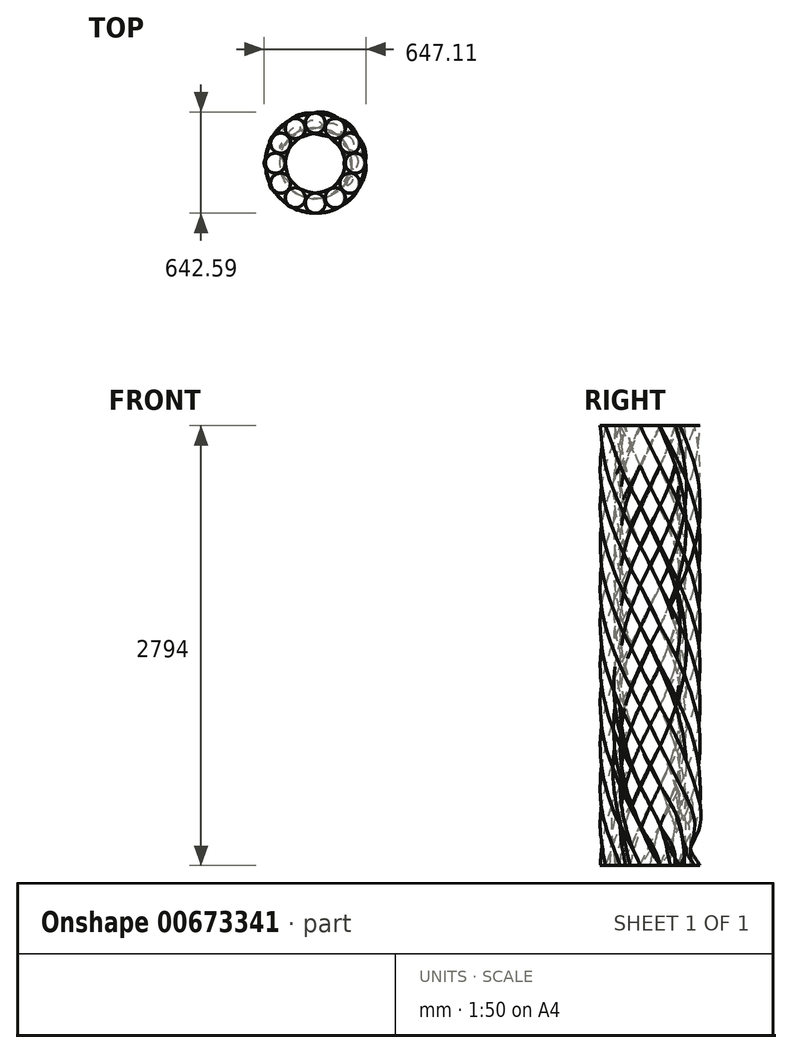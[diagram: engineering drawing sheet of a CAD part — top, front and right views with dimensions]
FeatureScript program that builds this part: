
annotation { "Feature Type Name" : "Feature", "Feature Type Description" : "" }
export const myFeature = defineFeature(function(context is Context, id is Id, definition is map)
    precondition{}
    {
        {
            var Q0;
            Q0=qCreatedBy(makeId("Top.planeOp"),FACE);
            cPlane(context, id + "F0", {"entities" : qUnion([Q0]), "cplaneType" : CPlaneType.OFFSET, "offset" : 254 * mm, "width" : 152.4 * mm, "height" : 152.4 * mm});
        }
        {
            var Q0;
            Q0=qCreatedBy(id+"F0.planeOp",FACE);
            cPlane(context, id + "F1", {"entities" : qUnion([Q0]), "cplaneType" : CPlaneType.OFFSET, "offset" : 254 * mm, "width" : 152.4 * mm, "height" : 152.4 * mm});
        }
        {
            var Q0;
            Q0=qCreatedBy(id+"F1.planeOp",FACE);
            cPlane(context, id + "F2", {"entities" : qUnion([Q0]), "cplaneType" : CPlaneType.OFFSET, "offset" : 254 * mm, "width" : 152.4 * mm, "height" : 152.4 * mm});
        }
        {
            var Q0;
            Q0=qCreatedBy(id+"F2.planeOp",FACE);
            cPlane(context, id + "F3", {"entities" : qUnion([Q0]), "cplaneType" : CPlaneType.OFFSET, "offset" : 254 * mm, "width" : 152.4 * mm, "height" : 152.4 * mm});
        }
        {
            var Q0;
            Q0=qCreatedBy(id+"F3.planeOp",FACE);
            cPlane(context, id + "F4", {"entities" : qUnion([Q0]), "cplaneType" : CPlaneType.OFFSET, "offset" : 254 * mm, "width" : 152.4 * mm, "height" : 152.4 * mm});
        }
        {
            var Q0;
            Q0=qCreatedBy(id+"F4.planeOp",FACE);
            cPlane(context, id + "F5", {"entities" : qUnion([Q0]), "cplaneType" : CPlaneType.OFFSET, "offset" : 254 * mm, "width" : 152.4 * mm, "height" : 152.4 * mm});
        }
        {
            var Q0;
            Q0=qCreatedBy(id+"F5.planeOp",FACE);
            cPlane(context, id + "F6", {"entities" : qUnion([Q0]), "cplaneType" : CPlaneType.OFFSET, "offset" : 254 * mm, "width" : 152.4 * mm, "height" : 152.4 * mm});
        }
        {
            var Q0;
            Q0=qCreatedBy(id+"F6.planeOp",FACE);
            cPlane(context, id + "F7", {"entities" : qUnion([Q0]), "cplaneType" : CPlaneType.OFFSET, "offset" : 254 * mm, "width" : 152.4 * mm, "height" : 152.4 * mm});
        }
        {
            var Q0;
            Q0=qCreatedBy(id+"F7.planeOp",FACE);
            cPlane(context, id + "F8", {"entities" : qUnion([Q0]), "cplaneType" : CPlaneType.OFFSET, "offset" : 254 * mm, "width" : 152.4 * mm, "height" : 152.4 * mm});
        }
        {
            var Q0;
            Q0=qCreatedBy(id+"F8.planeOp",FACE);
            cPlane(context, id + "F9", {"entities" : qUnion([Q0]), "cplaneType" : CPlaneType.OFFSET, "offset" : 254 * mm, "width" : 152.4 * mm, "height" : 152.4 * mm});
        }
        {
            var Q0;
            Q0=qCreatedBy(id+"F9.planeOp",FACE);
            cPlane(context, id + "F10", {"entities" : qUnion([Q0]), "cplaneType" : CPlaneType.OFFSET, "offset" : 254 * mm, "width" : 152.4 * mm, "height" : 152.4 * mm});
        }
        {
            var Q0;
            Q0=qCreatedBy(makeId("Top.planeOp"),FACE);
            var sketch = newSketch(context, id + "F11", { "sketchPlane" : qUnion([Q0])});
            skCircle(sketch, "E0", {"center": v(0, 0) * mm, "radius": 254 * mm, "construction": true});
            skLineSegment(sketch, "E1", {"start": v(13.76, 0) * mm, "end": v(-254, 0) * mm, "construction": true});
            skCircle(sketch, "E2", {"center": v(-254, 0) * mm, "radius": 63.5 * mm});
            skCircle(sketch, "E3.1.0", {"center": v(-219.97, -127) * mm, "radius": 63.5 * mm});
            skCircle(sketch, "E3.2.0", {"center": v(-127, -219.97) * mm, "radius": 63.5 * mm});
            skCircle(sketch, "E4.1.3.0", {"center": v(0, -254) * mm, "radius": 63.5 * mm});
            skCircle(sketch, "E4.1.4.0", {"center": v(127, -219.97) * mm, "radius": 63.5 * mm});
            skCircle(sketch, "E4.1.5.0", {"center": v(219.97, -127) * mm, "radius": 63.5 * mm});
            skCircle(sketch, "E4.1.6.0", {"center": v(254, 0) * mm, "radius": 63.5 * mm});
            skCircle(sketch, "E4.1.7.0", {"center": v(219.97, 127) * mm, "radius": 63.5 * mm});
            skCircle(sketch, "E4.1.8.0", {"center": v(127, 219.97) * mm, "radius": 63.5 * mm});
            skCircle(sketch, "E4.1.9.0", {"center": v(0, 254) * mm, "radius": 63.5 * mm});
            skCircle(sketch, "E4.1.10.0", {"center": v(-127, 219.97) * mm, "radius": 63.5 * mm});
            skCircle(sketch, "E4.1.11.0", {"center": v(-219.97, 127) * mm, "radius": 63.5 * mm});
            skSolve(sketch);
        }
        {
            var Q0;
            Q0=qCreatedBy(id+"F0.planeOp",FACE);
            var sketch = newSketch(context, id + "F12", { "sketchPlane" : qUnion([Q0])});
            skCircle(sketch, "E5", {"center": v(8, 0) * mm, "radius": 254 * mm, "construction": true});
            skLineSegment(sketch, "E6", {"start": v(21.76, 0) * mm, "end": v(-246, 0) * mm, "construction": true});
            skCircle(sketch, "E7", {"center": v(-246, 0) * mm, "radius": 63.5 * mm});
            skCircle(sketch, "E8.1.0", {"center": v(-211.96, -127) * mm, "radius": 63.5 * mm});
            skCircle(sketch, "E8.2.0", {"center": v(-119, -219.97) * mm, "radius": 63.5 * mm});
            skCircle(sketch, "E9.1.3.0", {"center": v(8, -254) * mm, "radius": 63.5 * mm});
            skCircle(sketch, "E9.1.4.0", {"center": v(135, -219.97) * mm, "radius": 63.5 * mm});
            skCircle(sketch, "E9.1.5.0", {"center": v(227.98, -127) * mm, "radius": 63.5 * mm});
            skCircle(sketch, "E9.1.6.0", {"center": v(262, 0) * mm, "radius": 63.5 * mm});
            skCircle(sketch, "E9.1.7.0", {"center": v(227.98, 127) * mm, "radius": 63.5 * mm});
            skCircle(sketch, "E9.1.8.0", {"center": v(135, 219.97) * mm, "radius": 63.5 * mm});
            skCircle(sketch, "E9.1.9.0", {"center": v(8, 254) * mm, "radius": 63.5 * mm});
            skCircle(sketch, "E9.1.10.0", {"center": v(-119, 219.97) * mm, "radius": 63.5 * mm});
            skCircle(sketch, "E9.1.11.0", {"center": v(-211.96, 127) * mm, "radius": 63.5 * mm});
            skSolve(sketch);
        }
        {
            var Q0;
            Q0=qCreatedBy(id+"F1.planeOp",FACE);
            var sketch = newSketch(context, id + "F13", { "sketchPlane" : qUnion([Q0])});
            skCircle(sketch, "E10", {"center": v(8, 0) * mm, "radius": 254 * mm, "construction": true});
            skLineSegment(sketch, "E11", {"start": v(21.76, 0) * mm, "end": v(-246, 0) * mm, "construction": true});
            skCircle(sketch, "E12", {"center": v(-246, 0) * mm, "radius": 63.5 * mm});
            skCircle(sketch, "E13.1.0", {"center": v(-211.96, -127) * mm, "radius": 63.5 * mm});
            skCircle(sketch, "E13.2.0", {"center": v(-119, -219.97) * mm, "radius": 63.5 * mm});
            skCircle(sketch, "E14.1.3.0", {"center": v(8, -254) * mm, "radius": 63.5 * mm});
            skCircle(sketch, "E14.1.4.0", {"center": v(135, -219.97) * mm, "radius": 63.5 * mm});
            skCircle(sketch, "E14.1.5.0", {"center": v(227.98, -127) * mm, "radius": 63.5 * mm});
            skCircle(sketch, "E14.1.6.0", {"center": v(262, 0) * mm, "radius": 63.5 * mm});
            skCircle(sketch, "E14.1.7.0", {"center": v(227.98, 127) * mm, "radius": 63.5 * mm});
            skCircle(sketch, "E14.1.8.0", {"center": v(135, 219.97) * mm, "radius": 63.5 * mm});
            skCircle(sketch, "E14.1.9.0", {"center": v(8, 254) * mm, "radius": 63.5 * mm});
            skCircle(sketch, "E14.1.10.0", {"center": v(-119, 219.97) * mm, "radius": 63.5 * mm});
            skCircle(sketch, "E14.1.11.0", {"center": v(-211.96, 127) * mm, "radius": 63.5 * mm});
            skSolve(sketch);
        }
        {
            var Q0;
            Q0=qCreatedBy(id+"F2.planeOp",FACE);
            var sketch = newSketch(context, id + "F14", { "sketchPlane" : qUnion([Q0])});
            skCircle(sketch, "E15", {"center": v(8, 0) * mm, "radius": 254 * mm, "construction": true});
            skLineSegment(sketch, "E16", {"start": v(21.76, 0) * mm, "end": v(-246, 0) * mm, "construction": true});
            skCircle(sketch, "E17", {"center": v(-246, 0) * mm, "radius": 63.5 * mm});
            skCircle(sketch, "E18.1.0", {"center": v(-211.96, -127) * mm, "radius": 63.5 * mm});
            skCircle(sketch, "E18.2.0", {"center": v(-119, -219.97) * mm, "radius": 63.5 * mm});
            skCircle(sketch, "E19.1.3.0", {"center": v(8, -254) * mm, "radius": 63.5 * mm});
            skCircle(sketch, "E19.1.4.0", {"center": v(135, -219.97) * mm, "radius": 63.5 * mm});
            skCircle(sketch, "E19.1.5.0", {"center": v(227.98, -127) * mm, "radius": 63.5 * mm});
            skCircle(sketch, "E19.1.6.0", {"center": v(262, 0) * mm, "radius": 63.5 * mm});
            skCircle(sketch, "E19.1.7.0", {"center": v(227.98, 127) * mm, "radius": 63.5 * mm});
            skCircle(sketch, "E19.1.8.0", {"center": v(135, 219.97) * mm, "radius": 63.5 * mm});
            skCircle(sketch, "E19.1.9.0", {"center": v(8, 254) * mm, "radius": 63.5 * mm});
            skCircle(sketch, "E19.1.10.0", {"center": v(-119, 219.97) * mm, "radius": 63.5 * mm});
            skCircle(sketch, "E19.1.11.0", {"center": v(-211.96, 127) * mm, "radius": 63.5 * mm});
            skSolve(sketch);
        }
        {
            var Q0;
            Q0=qCreatedBy(id+"F3.planeOp",FACE);
            var sketch = newSketch(context, id + "F15", { "sketchPlane" : qUnion([Q0])});
            skCircle(sketch, "E20", {"center": v(8, 0) * mm, "radius": 254 * mm, "construction": true});
            skLineSegment(sketch, "E21", {"start": v(21.76, 0) * mm, "end": v(-246, 0) * mm, "construction": true});
            skCircle(sketch, "E22", {"center": v(-246, 0) * mm, "radius": 63.5 * mm});
            skCircle(sketch, "E23.1.0", {"center": v(-211.96, -127) * mm, "radius": 63.5 * mm});
            skCircle(sketch, "E23.2.0", {"center": v(-119, -219.97) * mm, "radius": 63.5 * mm});
            skCircle(sketch, "E24.1.3.0", {"center": v(8, -254) * mm, "radius": 63.5 * mm});
            skCircle(sketch, "E24.1.4.0", {"center": v(135, -219.97) * mm, "radius": 63.5 * mm});
            skCircle(sketch, "E24.1.5.0", {"center": v(227.98, -127) * mm, "radius": 63.5 * mm});
            skCircle(sketch, "E24.1.6.0", {"center": v(262, 0) * mm, "radius": 63.5 * mm});
            skCircle(sketch, "E24.1.7.0", {"center": v(227.98, 127) * mm, "radius": 63.5 * mm});
            skCircle(sketch, "E24.1.8.0", {"center": v(135, 219.97) * mm, "radius": 63.5 * mm});
            skCircle(sketch, "E24.1.9.0", {"center": v(8, 254) * mm, "radius": 63.5 * mm});
            skCircle(sketch, "E24.1.10.0", {"center": v(-119, 219.97) * mm, "radius": 63.5 * mm});
            skCircle(sketch, "E24.1.11.0", {"center": v(-211.96, 127) * mm, "radius": 63.5 * mm});
            skSolve(sketch);
        }
        {
            var Q0;
            Q0=qCreatedBy(id+"F4.planeOp",FACE);
            var sketch = newSketch(context, id + "F16", { "sketchPlane" : qUnion([Q0])});
            skCircle(sketch, "E25", {"center": v(8, 0) * mm, "radius": 254 * mm, "construction": true});
            skLineSegment(sketch, "E26", {"start": v(21.76, 0) * mm, "end": v(-246, 0) * mm, "construction": true});
            skCircle(sketch, "E27", {"center": v(-246, 0) * mm, "radius": 63.5 * mm});
            skCircle(sketch, "E28.1.0", {"center": v(-211.96, -127) * mm, "radius": 63.5 * mm});
            skCircle(sketch, "E28.2.0", {"center": v(-119, -219.97) * mm, "radius": 63.5 * mm});
            skCircle(sketch, "E29.1.3.0", {"center": v(8, -254) * mm, "radius": 63.5 * mm});
            skCircle(sketch, "E29.1.4.0", {"center": v(135, -219.97) * mm, "radius": 63.5 * mm});
            skCircle(sketch, "E29.1.5.0", {"center": v(227.98, -127) * mm, "radius": 63.5 * mm});
            skCircle(sketch, "E29.1.6.0", {"center": v(262, 0) * mm, "radius": 63.5 * mm});
            skCircle(sketch, "E29.1.7.0", {"center": v(227.98, 127) * mm, "radius": 63.5 * mm});
            skCircle(sketch, "E29.1.8.0", {"center": v(135, 219.97) * mm, "radius": 63.5 * mm});
            skCircle(sketch, "E29.1.9.0", {"center": v(8, 254) * mm, "radius": 63.5 * mm});
            skCircle(sketch, "E29.1.10.0", {"center": v(-119, 219.97) * mm, "radius": 63.5 * mm});
            skCircle(sketch, "E29.1.11.0", {"center": v(-211.96, 127) * mm, "radius": 63.5 * mm});
            skSolve(sketch);
        }
        {
            var Q0;
            Q0=qCreatedBy(id+"F5.planeOp",FACE);
            var sketch = newSketch(context, id + "F17", { "sketchPlane" : qUnion([Q0])});
            skCircle(sketch, "E30", {"center": v(8, 0) * mm, "radius": 254 * mm, "construction": true});
            skLineSegment(sketch, "E31", {"start": v(21.76, 0) * mm, "end": v(-246, 0) * mm, "construction": true});
            skCircle(sketch, "E32", {"center": v(-246, 0) * mm, "radius": 63.5 * mm});
            skCircle(sketch, "E33.1.0", {"center": v(-211.96, -127) * mm, "radius": 63.5 * mm});
            skCircle(sketch, "E33.2.0", {"center": v(-119, -219.97) * mm, "radius": 63.5 * mm});
            skCircle(sketch, "E34.1.3.0", {"center": v(8, -254) * mm, "radius": 63.5 * mm});
            skCircle(sketch, "E34.1.4.0", {"center": v(135, -219.97) * mm, "radius": 63.5 * mm});
            skCircle(sketch, "E34.1.5.0", {"center": v(227.98, -127) * mm, "radius": 63.5 * mm});
            skCircle(sketch, "E34.1.6.0", {"center": v(262, 0) * mm, "radius": 63.5 * mm});
            skCircle(sketch, "E34.1.7.0", {"center": v(227.98, 127) * mm, "radius": 63.5 * mm});
            skCircle(sketch, "E34.1.8.0", {"center": v(135, 219.97) * mm, "radius": 63.5 * mm});
            skCircle(sketch, "E34.1.9.0", {"center": v(8, 254) * mm, "radius": 63.5 * mm});
            skCircle(sketch, "E34.1.10.0", {"center": v(-119, 219.97) * mm, "radius": 63.5 * mm});
            skCircle(sketch, "E34.1.11.0", {"center": v(-211.96, 127) * mm, "radius": 63.5 * mm});
            skSolve(sketch);
        }
        {
            var Q0;
            Q0=qCreatedBy(id+"F6.planeOp",FACE);
            var sketch = newSketch(context, id + "F18", { "sketchPlane" : qUnion([Q0])});
            skCircle(sketch, "E35", {"center": v(8, 0) * mm, "radius": 254 * mm, "construction": true});
            skLineSegment(sketch, "E36", {"start": v(21.76, 0) * mm, "end": v(-246, 0) * mm, "construction": true});
            skCircle(sketch, "E37", {"center": v(-246, 0) * mm, "radius": 63.5 * mm});
            skCircle(sketch, "E38.1.0", {"center": v(-211.96, -127) * mm, "radius": 63.5 * mm});
            skCircle(sketch, "E38.2.0", {"center": v(-119, -219.97) * mm, "radius": 63.5 * mm});
            skCircle(sketch, "E39.1.3.0", {"center": v(8, -254) * mm, "radius": 63.5 * mm});
            skCircle(sketch, "E39.1.4.0", {"center": v(135, -219.97) * mm, "radius": 63.5 * mm});
            skCircle(sketch, "E39.1.5.0", {"center": v(227.98, -127) * mm, "radius": 63.5 * mm});
            skCircle(sketch, "E39.1.6.0", {"center": v(262, 0) * mm, "radius": 63.5 * mm});
            skCircle(sketch, "E39.1.7.0", {"center": v(227.98, 127) * mm, "radius": 63.5 * mm});
            skCircle(sketch, "E39.1.8.0", {"center": v(135, 219.97) * mm, "radius": 63.5 * mm});
            skCircle(sketch, "E39.1.9.0", {"center": v(8, 254) * mm, "radius": 63.5 * mm});
            skCircle(sketch, "E39.1.10.0", {"center": v(-119, 219.97) * mm, "radius": 63.5 * mm});
            skCircle(sketch, "E39.1.11.0", {"center": v(-211.96, 127) * mm, "radius": 63.5 * mm});
            skSolve(sketch);
        }
        {
            var Q0;
            Q0=qCreatedBy(id+"F7.planeOp",FACE);
            var sketch = newSketch(context, id + "F19", { "sketchPlane" : qUnion([Q0])});
            skCircle(sketch, "E40", {"center": v(8, 0) * mm, "radius": 254 * mm, "construction": true});
            skLineSegment(sketch, "E41", {"start": v(21.76, 0) * mm, "end": v(-246, 0) * mm, "construction": true});
            skCircle(sketch, "E42", {"center": v(-246, 0) * mm, "radius": 63.5 * mm});
            skCircle(sketch, "E43.1.0", {"center": v(-211.96, -127) * mm, "radius": 63.5 * mm});
            skCircle(sketch, "E43.2.0", {"center": v(-119, -219.97) * mm, "radius": 63.5 * mm});
            skCircle(sketch, "E44.1.3.0", {"center": v(8, -254) * mm, "radius": 63.5 * mm});
            skCircle(sketch, "E44.1.4.0", {"center": v(135, -219.97) * mm, "radius": 63.5 * mm});
            skCircle(sketch, "E44.1.5.0", {"center": v(227.98, -127) * mm, "radius": 63.5 * mm});
            skCircle(sketch, "E44.1.6.0", {"center": v(262, 0) * mm, "radius": 63.5 * mm});
            skCircle(sketch, "E44.1.7.0", {"center": v(227.98, 127) * mm, "radius": 63.5 * mm});
            skCircle(sketch, "E44.1.8.0", {"center": v(135, 219.97) * mm, "radius": 63.5 * mm});
            skCircle(sketch, "E44.1.9.0", {"center": v(8, 254) * mm, "radius": 63.5 * mm});
            skCircle(sketch, "E44.1.10.0", {"center": v(-119, 219.97) * mm, "radius": 63.5 * mm});
            skCircle(sketch, "E44.1.11.0", {"center": v(-211.96, 127) * mm, "radius": 63.5 * mm});
            skSolve(sketch);
        }
        {
            var Q0;
            Q0=qCreatedBy(id+"F8.planeOp",FACE);
            var sketch = newSketch(context, id + "F20", { "sketchPlane" : qUnion([Q0])});
            skCircle(sketch, "E45", {"center": v(8, 0) * mm, "radius": 254 * mm, "construction": true});
            skLineSegment(sketch, "E46", {"start": v(21.76, 0) * mm, "end": v(-246, 0) * mm, "construction": true});
            skCircle(sketch, "E47", {"center": v(-246, 0) * mm, "radius": 63.5 * mm});
            skCircle(sketch, "E48.1.0", {"center": v(-211.96, -127) * mm, "radius": 63.5 * mm});
            skCircle(sketch, "E48.2.0", {"center": v(-119, -219.97) * mm, "radius": 63.5 * mm});
            skCircle(sketch, "E49.1.3.0", {"center": v(8, -254) * mm, "radius": 63.5 * mm});
            skCircle(sketch, "E49.1.4.0", {"center": v(135, -219.97) * mm, "radius": 63.5 * mm});
            skCircle(sketch, "E49.1.5.0", {"center": v(227.98, -127) * mm, "radius": 63.5 * mm});
            skCircle(sketch, "E49.1.6.0", {"center": v(262, 0) * mm, "radius": 63.5 * mm});
            skCircle(sketch, "E49.1.7.0", {"center": v(227.98, 127) * mm, "radius": 63.5 * mm});
            skCircle(sketch, "E49.1.8.0", {"center": v(135, 219.97) * mm, "radius": 63.5 * mm});
            skCircle(sketch, "E49.1.9.0", {"center": v(8, 254) * mm, "radius": 63.5 * mm});
            skCircle(sketch, "E49.1.10.0", {"center": v(-119, 219.97) * mm, "radius": 63.5 * mm});
            skCircle(sketch, "E49.1.11.0", {"center": v(-211.96, 127) * mm, "radius": 63.5 * mm});
            skSolve(sketch);
        }
        {
            var Q0;
            Q0=qCreatedBy(id+"F9.planeOp",FACE);
            var sketch = newSketch(context, id + "F21", { "sketchPlane" : qUnion([Q0])});
            skCircle(sketch, "E50", {"center": v(8, 0) * mm, "radius": 254 * mm, "construction": true});
            skLineSegment(sketch, "E51", {"start": v(21.76, 0) * mm, "end": v(-246, 0) * mm, "construction": true});
            skCircle(sketch, "E52", {"center": v(-246, 0) * mm, "radius": 63.5 * mm});
            skCircle(sketch, "E53.1.0", {"center": v(-211.96, -127) * mm, "radius": 63.5 * mm});
            skCircle(sketch, "E53.2.0", {"center": v(-119, -219.97) * mm, "radius": 63.5 * mm});
            skCircle(sketch, "E54.1.3.0", {"center": v(8, -254) * mm, "radius": 63.5 * mm});
            skCircle(sketch, "E54.1.4.0", {"center": v(135, -219.97) * mm, "radius": 63.5 * mm});
            skCircle(sketch, "E54.1.5.0", {"center": v(227.98, -127) * mm, "radius": 63.5 * mm});
            skCircle(sketch, "E54.1.6.0", {"center": v(262, 0) * mm, "radius": 63.5 * mm});
            skCircle(sketch, "E54.1.7.0", {"center": v(227.98, 127) * mm, "radius": 63.5 * mm});
            skCircle(sketch, "E54.1.8.0", {"center": v(135, 219.97) * mm, "radius": 63.5 * mm});
            skCircle(sketch, "E54.1.9.0", {"center": v(8, 254) * mm, "radius": 63.5 * mm});
            skCircle(sketch, "E54.1.10.0", {"center": v(-119, 219.97) * mm, "radius": 63.5 * mm});
            skCircle(sketch, "E54.1.11.0", {"center": v(-211.96, 127) * mm, "radius": 63.5 * mm});
            skSolve(sketch);
        }
        {
            var Q0;
            Q0=qCreatedBy(id+"F10.planeOp",FACE);
            var sketch = newSketch(context, id + "F22", { "sketchPlane" : qUnion([Q0])});
            skCircle(sketch, "E55", {"center": v(8, 0) * mm, "radius": 254 * mm, "construction": true});
            skLineSegment(sketch, "E56", {"start": v(21.76, 0) * mm, "end": v(-246, 0) * mm, "construction": true});
            skCircle(sketch, "E57", {"center": v(-246, 0) * mm, "radius": 63.5 * mm});
            skCircle(sketch, "E58.1.0", {"center": v(-211.96, -127) * mm, "radius": 63.5 * mm});
            skCircle(sketch, "E58.2.0", {"center": v(-119, -219.97) * mm, "radius": 63.5 * mm});
            skCircle(sketch, "E59.1.3.0", {"center": v(8, -254) * mm, "radius": 63.5 * mm});
            skCircle(sketch, "E59.1.4.0", {"center": v(135, -219.97) * mm, "radius": 63.5 * mm});
            skCircle(sketch, "E59.1.5.0", {"center": v(227.98, -127) * mm, "radius": 63.5 * mm});
            skCircle(sketch, "E59.1.6.0", {"center": v(262, 0) * mm, "radius": 63.5 * mm});
            skCircle(sketch, "E59.1.7.0", {"center": v(227.98, 127) * mm, "radius": 63.5 * mm});
            skCircle(sketch, "E59.1.8.0", {"center": v(135, 219.97) * mm, "radius": 63.5 * mm});
            skCircle(sketch, "E59.1.9.0", {"center": v(8, 254) * mm, "radius": 63.5 * mm});
            skCircle(sketch, "E59.1.10.0", {"center": v(-119, 219.97) * mm, "radius": 63.5 * mm});
            skCircle(sketch, "E59.1.11.0", {"center": v(-211.96, 127) * mm, "radius": 63.5 * mm});
            skSolve(sketch);
        }
        {
            var Q0;
            Q0=makeQuery(id+"F11.imprint","IMPRINT",FACE,{"disambiguationData":[TD([[makeQuery(id+"F11.imprint","IMPRINT",EDGE,{"derivedFrom":sQuery(id+"F11.wireOp",EDGE,"E2")}),1.0]])]});
            var Q1;
            Q1=makeQuery(id+"F12.imprint","IMPRINT",FACE,{"disambiguationData":[TD([[makeQuery(id+"F12.imprint","IMPRINT",EDGE,{"derivedFrom":sQuery(id+"F12.wireOp",EDGE,"E9.1.11.0")}),1.0]])]});
            var Q2;
            Q2=makeQuery(id+"F13.imprint","IMPRINT",FACE,{"disambiguationData":[TD([[makeQuery(id+"F13.imprint","IMPRINT",EDGE,{"derivedFrom":sQuery(id+"F13.wireOp",EDGE,"E14.1.10.0")}),1.0]])]});
            var Q3;
            Q3=makeQuery(id+"F14.imprint","IMPRINT",FACE,{"disambiguationData":[TD([[makeQuery(id+"F14.imprint","IMPRINT",EDGE,{"derivedFrom":sQuery(id+"F14.wireOp",EDGE,"E19.1.9.0")}),1.0]])]});
            var Q4;
            Q4=makeQuery(id+"F15.imprint","IMPRINT",FACE,{"disambiguationData":[TD([[makeQuery(id+"F15.imprint","IMPRINT",EDGE,{"derivedFrom":sQuery(id+"F15.wireOp",EDGE,"E24.1.8.0")}),1.0]])]});
            var Q5;
            Q5=makeQuery(id+"F16.imprint","IMPRINT",FACE,{"disambiguationData":[TD([[makeQuery(id+"F16.imprint","IMPRINT",EDGE,{"derivedFrom":sQuery(id+"F16.wireOp",EDGE,"E29.1.7.0")}),1.0]])]});
            var Q6;
            Q6=makeQuery(id+"F17.imprint","IMPRINT",FACE,{"disambiguationData":[TD([[makeQuery(id+"F17.imprint","IMPRINT",EDGE,{"derivedFrom":sQuery(id+"F17.wireOp",EDGE,"E34.1.6.0")}),1.0]])]});
            var Q7;
            Q7=makeQuery(id+"F18.imprint","IMPRINT",FACE,{"disambiguationData":[TD([[makeQuery(id+"F18.imprint","IMPRINT",EDGE,{"derivedFrom":sQuery(id+"F18.wireOp",EDGE,"E39.1.5.0")}),1.0]])]});
            var Q8;
            Q8=makeQuery(id+"F19.imprint","IMPRINT",FACE,{"disambiguationData":[TD([[makeQuery(id+"F19.imprint","IMPRINT",EDGE,{"derivedFrom":sQuery(id+"F19.wireOp",EDGE,"E44.1.4.0")}),1.0]])]});
            var Q9;
            Q9=makeQuery(id+"F20.imprint","IMPRINT",FACE,{"disambiguationData":[TD([[makeQuery(id+"F20.imprint","IMPRINT",EDGE,{"derivedFrom":sQuery(id+"F20.wireOp",EDGE,"E49.1.3.0")}),1.0]])]});
            var Q10;
            Q10=makeQuery(id+"F21.imprint","IMPRINT",FACE,{"disambiguationData":[TD([[makeQuery(id+"F21.imprint","IMPRINT",EDGE,{"derivedFrom":sQuery(id+"F21.wireOp",EDGE,"E53.2.0")}),1.0]])]});
            var Q11;
            Q11=makeQuery(id+"F22.imprint","IMPRINT",FACE,{"disambiguationData":[TD([[makeQuery(id+"F22.imprint","IMPRINT",EDGE,{"derivedFrom":sQuery(id+"F22.wireOp",EDGE,"E58.1.0")}),1.0]])]});
            loft(context, id + "F23", {"sheetProfilesArray" : [{ "sheetProfileEntities" : qUnion([Q0]) }, { "sheetProfileEntities" : qUnion([Q1]) }, { "sheetProfileEntities" : qUnion([Q2]) }, { "sheetProfileEntities" : qUnion([Q3]) }, { "sheetProfileEntities" : qUnion([Q4]) }, { "sheetProfileEntities" : qUnion([Q5]) }, { "sheetProfileEntities" : qUnion([Q6]) }, { "sheetProfileEntities" : qUnion([Q7]) }, { "sheetProfileEntities" : qUnion([Q8]) }, { "sheetProfileEntities" : qUnion([Q9]) }, { "sheetProfileEntities" : qUnion([Q10]) }, { "sheetProfileEntities" : qUnion([Q11]) }]});
        }
        {
            var Q1;
            Q1=makeQuery(id+"F11.imprint","IMPRINT",FACE,{"disambiguationData":[TD([[makeQuery(id+"F11.imprint","IMPRINT",EDGE,{"derivedFrom":sQuery(id+"F11.wireOp",EDGE,"E4.1.11.0")}),1.0]])]});
            var Q2;
            Q2=makeQuery(id+"F12.imprint","IMPRINT",FACE,{"disambiguationData":[TD([[makeQuery(id+"F12.imprint","IMPRINT",EDGE,{"derivedFrom":sQuery(id+"F12.wireOp",EDGE,"E9.1.10.0")}),1.0]])]});
            var Q3;
            Q3=makeQuery(id+"F13.imprint","IMPRINT",FACE,{"disambiguationData":[TD([[makeQuery(id+"F13.imprint","IMPRINT",EDGE,{"derivedFrom":sQuery(id+"F13.wireOp",EDGE,"E14.1.9.0")}),1.0]])]});
            var Q4;
            Q4=makeQuery(id+"F14.imprint","IMPRINT",FACE,{"disambiguationData":[TD([[makeQuery(id+"F14.imprint","IMPRINT",EDGE,{"derivedFrom":sQuery(id+"F14.wireOp",EDGE,"E19.1.8.0")}),1.0]])]});
            var Q5;
            Q5=makeQuery(id+"F15.imprint","IMPRINT",FACE,{"disambiguationData":[TD([[makeQuery(id+"F15.imprint","IMPRINT",EDGE,{"derivedFrom":sQuery(id+"F15.wireOp",EDGE,"E24.1.7.0")}),1.0]])]});
            var Q6;
            Q6=makeQuery(id+"F16.imprint","IMPRINT",FACE,{"disambiguationData":[TD([[makeQuery(id+"F16.imprint","IMPRINT",EDGE,{"derivedFrom":sQuery(id+"F16.wireOp",EDGE,"E29.1.6.0")}),1.0]])]});
            var Q7;
            Q7=makeQuery(id+"F17.imprint","IMPRINT",FACE,{"disambiguationData":[TD([[makeQuery(id+"F17.imprint","IMPRINT",EDGE,{"derivedFrom":sQuery(id+"F17.wireOp",EDGE,"E34.1.5.0")}),1.0]])]});
            var Q8;
            Q8=makeQuery(id+"F18.imprint","IMPRINT",FACE,{"disambiguationData":[TD([[makeQuery(id+"F18.imprint","IMPRINT",EDGE,{"derivedFrom":sQuery(id+"F18.wireOp",EDGE,"E39.1.4.0")}),1.0]])]});
            var Q9;
            Q9=makeQuery(id+"F19.imprint","IMPRINT",FACE,{"disambiguationData":[TD([[makeQuery(id+"F19.imprint","IMPRINT",EDGE,{"derivedFrom":sQuery(id+"F19.wireOp",EDGE,"E44.1.3.0")}),1.0]])]});
            var Q10;
            Q10=makeQuery(id+"F20.imprint","IMPRINT",FACE,{"disambiguationData":[TD([[makeQuery(id+"F20.imprint","IMPRINT",EDGE,{"derivedFrom":sQuery(id+"F20.wireOp",EDGE,"E48.2.0")}),1.0]])]});
            var Q11;
            Q11=makeQuery(id+"F21.imprint","IMPRINT",FACE,{"disambiguationData":[TD([[makeQuery(id+"F21.imprint","IMPRINT",EDGE,{"derivedFrom":sQuery(id+"F21.wireOp",EDGE,"E53.1.0")}),1.0]])]});
            var Q12;
            Q12=makeQuery(id+"F22.imprint","IMPRINT",FACE,{"disambiguationData":[TD([[makeQuery(id+"F22.imprint","IMPRINT",EDGE,{"derivedFrom":sQuery(id+"F22.wireOp",EDGE,"E57")}),1.0]])]});
            loft(context, id + "F24", {"operationType" : NewBodyOperationType.ADD, "sheetProfilesArray" : [{ "sheetProfileEntities" : qUnion([Q1]) }, { "sheetProfileEntities" : qUnion([Q2]) }, { "sheetProfileEntities" : qUnion([Q3]) }, { "sheetProfileEntities" : qUnion([Q4]) }, { "sheetProfileEntities" : qUnion([Q5]) }, { "sheetProfileEntities" : qUnion([Q6]) }, { "sheetProfileEntities" : qUnion([Q7]) }, { "sheetProfileEntities" : qUnion([Q8]) }, { "sheetProfileEntities" : qUnion([Q9]) }, { "sheetProfileEntities" : qUnion([Q10]) }, { "sheetProfileEntities" : qUnion([Q11]) }, { "sheetProfileEntities" : qUnion([Q12]) }]});
        }
        {
            var Q1;
            Q1=makeQuery(id+"F11.imprint","IMPRINT",FACE,{"disambiguationData":[TD([[makeQuery(id+"F11.imprint","IMPRINT",EDGE,{"derivedFrom":sQuery(id+"F11.wireOp",EDGE,"E4.1.10.0")}),1.0]])]});
            var Q2;
            Q2=makeQuery(id+"F12.imprint","IMPRINT",FACE,{"disambiguationData":[TD([[makeQuery(id+"F12.imprint","IMPRINT",EDGE,{"derivedFrom":sQuery(id+"F12.wireOp",EDGE,"E9.1.9.0")}),1.0]])]});
            var Q3;
            Q3=makeQuery(id+"F13.imprint","IMPRINT",FACE,{"disambiguationData":[TD([[makeQuery(id+"F13.imprint","IMPRINT",EDGE,{"derivedFrom":sQuery(id+"F13.wireOp",EDGE,"E14.1.8.0")}),1.0]])]});
            var Q4;
            Q4=makeQuery(id+"F14.imprint","IMPRINT",FACE,{"disambiguationData":[TD([[makeQuery(id+"F14.imprint","IMPRINT",EDGE,{"derivedFrom":sQuery(id+"F14.wireOp",EDGE,"E19.1.7.0")}),1.0]])]});
            var Q5;
            Q5=makeQuery(id+"F15.imprint","IMPRINT",FACE,{"disambiguationData":[TD([[makeQuery(id+"F15.imprint","IMPRINT",EDGE,{"derivedFrom":sQuery(id+"F15.wireOp",EDGE,"E24.1.6.0")}),1.0]])]});
            var Q6;
            Q6=makeQuery(id+"F16.imprint","IMPRINT",FACE,{"disambiguationData":[TD([[makeQuery(id+"F16.imprint","IMPRINT",EDGE,{"derivedFrom":sQuery(id+"F16.wireOp",EDGE,"E29.1.5.0")}),1.0]])]});
            var Q7;
            Q7=makeQuery(id+"F17.imprint","IMPRINT",FACE,{"disambiguationData":[TD([[makeQuery(id+"F17.imprint","IMPRINT",EDGE,{"derivedFrom":sQuery(id+"F17.wireOp",EDGE,"E34.1.4.0")}),1.0]])]});
            var Q8;
            Q8=makeQuery(id+"F18.imprint","IMPRINT",FACE,{"disambiguationData":[TD([[makeQuery(id+"F18.imprint","IMPRINT",EDGE,{"derivedFrom":sQuery(id+"F18.wireOp",EDGE,"E39.1.3.0")}),1.0]])]});
            var Q9;
            Q9=makeQuery(id+"F19.imprint","IMPRINT",FACE,{"disambiguationData":[TD([[makeQuery(id+"F19.imprint","IMPRINT",EDGE,{"derivedFrom":sQuery(id+"F19.wireOp",EDGE,"E43.2.0")}),1.0]])]});
            var Q10;
            Q10=makeQuery(id+"F20.imprint","IMPRINT",FACE,{"disambiguationData":[TD([[makeQuery(id+"F20.imprint","IMPRINT",EDGE,{"derivedFrom":sQuery(id+"F20.wireOp",EDGE,"E48.1.0")}),1.0]])]});
            var Q11;
            Q11=makeQuery(id+"F21.imprint","IMPRINT",FACE,{"disambiguationData":[TD([[makeQuery(id+"F21.imprint","IMPRINT",EDGE,{"derivedFrom":sQuery(id+"F21.wireOp",EDGE,"E52")}),1.0]])]});
            var Q12;
            Q12=makeQuery(id+"F22.imprint","IMPRINT",FACE,{"disambiguationData":[TD([[makeQuery(id+"F22.imprint","IMPRINT",EDGE,{"derivedFrom":sQuery(id+"F22.wireOp",EDGE,"E59.1.11.0")}),1.0]])]});
            loft(context, id + "F25", {"operationType" : NewBodyOperationType.ADD, "sheetProfilesArray" : [{ "sheetProfileEntities" : qUnion([Q1]) }, { "sheetProfileEntities" : qUnion([Q2]) }, { "sheetProfileEntities" : qUnion([Q3]) }, { "sheetProfileEntities" : qUnion([Q4]) }, { "sheetProfileEntities" : qUnion([Q5]) }, { "sheetProfileEntities" : qUnion([Q6]) }, { "sheetProfileEntities" : qUnion([Q7]) }, { "sheetProfileEntities" : qUnion([Q8]) }, { "sheetProfileEntities" : qUnion([Q9]) }, { "sheetProfileEntities" : qUnion([Q10]) }, { "sheetProfileEntities" : qUnion([Q11]) }, { "sheetProfileEntities" : qUnion([Q12]) }]});
        }
        {
            var Q1;
            Q1=makeQuery(id+"F11.imprint","IMPRINT",FACE,{"disambiguationData":[TD([[makeQuery(id+"F11.imprint","IMPRINT",EDGE,{"derivedFrom":sQuery(id+"F11.wireOp",EDGE,"E4.1.9.0")}),1.0]])]});
            var Q2;
            Q2=makeQuery(id+"F12.imprint","IMPRINT",FACE,{"disambiguationData":[TD([[makeQuery(id+"F12.imprint","IMPRINT",EDGE,{"derivedFrom":sQuery(id+"F12.wireOp",EDGE,"E9.1.8.0")}),1.0]])]});
            var Q3;
            Q3=makeQuery(id+"F13.imprint","IMPRINT",FACE,{"disambiguationData":[TD([[makeQuery(id+"F13.imprint","IMPRINT",EDGE,{"derivedFrom":sQuery(id+"F13.wireOp",EDGE,"E14.1.7.0")}),1.0]])]});
            var Q4;
            Q4=makeQuery(id+"F14.imprint","IMPRINT",FACE,{"disambiguationData":[TD([[makeQuery(id+"F14.imprint","IMPRINT",EDGE,{"derivedFrom":sQuery(id+"F14.wireOp",EDGE,"E19.1.6.0")}),1.0]])]});
            var Q5;
            Q5=makeQuery(id+"F15.imprint","IMPRINT",FACE,{"disambiguationData":[TD([[makeQuery(id+"F15.imprint","IMPRINT",EDGE,{"derivedFrom":sQuery(id+"F15.wireOp",EDGE,"E24.1.5.0")}),1.0]])]});
            var Q6;
            Q6=makeQuery(id+"F16.imprint","IMPRINT",FACE,{"disambiguationData":[TD([[makeQuery(id+"F16.imprint","IMPRINT",EDGE,{"derivedFrom":sQuery(id+"F16.wireOp",EDGE,"E29.1.4.0")}),1.0]])]});
            var Q7;
            Q7=makeQuery(id+"F17.imprint","IMPRINT",FACE,{"disambiguationData":[TD([[makeQuery(id+"F17.imprint","IMPRINT",EDGE,{"derivedFrom":sQuery(id+"F17.wireOp",EDGE,"E34.1.3.0")}),1.0]])]});
            var Q8;
            Q8=makeQuery(id+"F18.imprint","IMPRINT",FACE,{"disambiguationData":[TD([[makeQuery(id+"F18.imprint","IMPRINT",EDGE,{"derivedFrom":sQuery(id+"F18.wireOp",EDGE,"E38.2.0")}),1.0]])]});
            var Q9;
            Q9=makeQuery(id+"F19.imprint","IMPRINT",FACE,{"disambiguationData":[TD([[makeQuery(id+"F19.imprint","IMPRINT",EDGE,{"derivedFrom":sQuery(id+"F19.wireOp",EDGE,"E43.1.0")}),1.0]])]});
            var Q10;
            Q10=makeQuery(id+"F20.imprint","IMPRINT",FACE,{"disambiguationData":[TD([[makeQuery(id+"F20.imprint","IMPRINT",EDGE,{"derivedFrom":sQuery(id+"F20.wireOp",EDGE,"E47")}),1.0]])]});
            var Q11;
            Q11=makeQuery(id+"F21.imprint","IMPRINT",FACE,{"disambiguationData":[TD([[makeQuery(id+"F21.imprint","IMPRINT",EDGE,{"derivedFrom":sQuery(id+"F21.wireOp",EDGE,"E54.1.11.0")}),1.0]])]});
            var Q12;
            Q12=makeQuery(id+"F22.imprint","IMPRINT",FACE,{"disambiguationData":[TD([[makeQuery(id+"F22.imprint","IMPRINT",EDGE,{"derivedFrom":sQuery(id+"F22.wireOp",EDGE,"E59.1.10.0")}),1.0]])]});
            loft(context, id + "F26", {"operationType" : NewBodyOperationType.ADD, "sheetProfilesArray" : [{ "sheetProfileEntities" : qUnion([Q1]) }, { "sheetProfileEntities" : qUnion([Q2]) }, { "sheetProfileEntities" : qUnion([Q3]) }, { "sheetProfileEntities" : qUnion([Q4]) }, { "sheetProfileEntities" : qUnion([Q5]) }, { "sheetProfileEntities" : qUnion([Q6]) }, { "sheetProfileEntities" : qUnion([Q7]) }, { "sheetProfileEntities" : qUnion([Q8]) }, { "sheetProfileEntities" : qUnion([Q9]) }, { "sheetProfileEntities" : qUnion([Q10]) }, { "sheetProfileEntities" : qUnion([Q11]) }, { "sheetProfileEntities" : qUnion([Q12]) }]});
        }
        {
            var Q1;
            Q1=makeQuery(id+"F11.imprint","IMPRINT",FACE,{"disambiguationData":[TD([[makeQuery(id+"F11.imprint","IMPRINT",EDGE,{"derivedFrom":sQuery(id+"F11.wireOp",EDGE,"E4.1.8.0")}),1.0]])]});
            var Q2;
            Q2=makeQuery(id+"F12.imprint","IMPRINT",FACE,{"disambiguationData":[TD([[makeQuery(id+"F12.imprint","IMPRINT",EDGE,{"derivedFrom":sQuery(id+"F12.wireOp",EDGE,"E9.1.7.0")}),1.0]])]});
            var Q3;
            Q3=makeQuery(id+"F13.imprint","IMPRINT",FACE,{"disambiguationData":[TD([[makeQuery(id+"F13.imprint","IMPRINT",EDGE,{"derivedFrom":sQuery(id+"F13.wireOp",EDGE,"E14.1.6.0")}),1.0]])]});
            var Q4;
            Q4=makeQuery(id+"F14.imprint","IMPRINT",FACE,{"disambiguationData":[TD([[makeQuery(id+"F14.imprint","IMPRINT",EDGE,{"derivedFrom":sQuery(id+"F14.wireOp",EDGE,"E19.1.5.0")}),1.0]])]});
            var Q5;
            Q5=makeQuery(id+"F15.imprint","IMPRINT",FACE,{"disambiguationData":[TD([[makeQuery(id+"F15.imprint","IMPRINT",EDGE,{"derivedFrom":sQuery(id+"F15.wireOp",EDGE,"E24.1.4.0")}),1.0]])]});
            var Q6;
            Q6=makeQuery(id+"F16.imprint","IMPRINT",FACE,{"disambiguationData":[TD([[makeQuery(id+"F16.imprint","IMPRINT",EDGE,{"derivedFrom":sQuery(id+"F16.wireOp",EDGE,"E29.1.3.0")}),1.0]])]});
            var Q7;
            Q7=makeQuery(id+"F17.imprint","IMPRINT",FACE,{"disambiguationData":[TD([[makeQuery(id+"F17.imprint","IMPRINT",EDGE,{"derivedFrom":sQuery(id+"F17.wireOp",EDGE,"E33.2.0")}),1.0]])]});
            var Q8;
            Q8=makeQuery(id+"F18.imprint","IMPRINT",FACE,{"disambiguationData":[TD([[makeQuery(id+"F18.imprint","IMPRINT",EDGE,{"derivedFrom":sQuery(id+"F18.wireOp",EDGE,"E38.1.0")}),1.0]])]});
            var Q9;
            Q9=makeQuery(id+"F19.imprint","IMPRINT",FACE,{"disambiguationData":[TD([[makeQuery(id+"F19.imprint","IMPRINT",EDGE,{"derivedFrom":sQuery(id+"F19.wireOp",EDGE,"E42")}),1.0]])]});
            var Q10;
            Q10=makeQuery(id+"F20.imprint","IMPRINT",FACE,{"disambiguationData":[TD([[makeQuery(id+"F20.imprint","IMPRINT",EDGE,{"derivedFrom":sQuery(id+"F20.wireOp",EDGE,"E49.1.11.0")}),1.0]])]});
            var Q11;
            Q11=makeQuery(id+"F21.imprint","IMPRINT",FACE,{"disambiguationData":[TD([[makeQuery(id+"F21.imprint","IMPRINT",EDGE,{"derivedFrom":sQuery(id+"F21.wireOp",EDGE,"E54.1.10.0")}),1.0]])]});
            var Q12;
            Q12=makeQuery(id+"F22.imprint","IMPRINT",FACE,{"disambiguationData":[TD([[makeQuery(id+"F22.imprint","IMPRINT",EDGE,{"derivedFrom":sQuery(id+"F22.wireOp",EDGE,"E59.1.9.0")}),1.0]])]});
            loft(context, id + "F27", {"operationType" : NewBodyOperationType.ADD, "sheetProfilesArray" : [{ "sheetProfileEntities" : qUnion([Q1]) }, { "sheetProfileEntities" : qUnion([Q2]) }, { "sheetProfileEntities" : qUnion([Q3]) }, { "sheetProfileEntities" : qUnion([Q4]) }, { "sheetProfileEntities" : qUnion([Q5]) }, { "sheetProfileEntities" : qUnion([Q6]) }, { "sheetProfileEntities" : qUnion([Q7]) }, { "sheetProfileEntities" : qUnion([Q8]) }, { "sheetProfileEntities" : qUnion([Q9]) }, { "sheetProfileEntities" : qUnion([Q10]) }, { "sheetProfileEntities" : qUnion([Q11]) }, { "sheetProfileEntities" : qUnion([Q12]) }]});
        }
        {
            var Q1;
            Q1=makeQuery(id+"F11.imprint","IMPRINT",FACE,{"disambiguationData":[TD([[makeQuery(id+"F11.imprint","IMPRINT",EDGE,{"derivedFrom":sQuery(id+"F11.wireOp",EDGE,"E4.1.7.0")}),1.0]])]});
            var Q2;
            Q2=makeQuery(id+"F12.imprint","IMPRINT",FACE,{"disambiguationData":[TD([[makeQuery(id+"F12.imprint","IMPRINT",EDGE,{"derivedFrom":sQuery(id+"F12.wireOp",EDGE,"E9.1.6.0")}),1.0]])]});
            var Q3;
            Q3=makeQuery(id+"F13.imprint","IMPRINT",FACE,{"disambiguationData":[TD([[makeQuery(id+"F13.imprint","IMPRINT",EDGE,{"derivedFrom":sQuery(id+"F13.wireOp",EDGE,"E14.1.5.0")}),1.0]])]});
            var Q4;
            Q4=makeQuery(id+"F14.imprint","IMPRINT",FACE,{"disambiguationData":[TD([[makeQuery(id+"F14.imprint","IMPRINT",EDGE,{"derivedFrom":sQuery(id+"F14.wireOp",EDGE,"E19.1.4.0")}),1.0]])]});
            var Q5;
            Q5=makeQuery(id+"F15.imprint","IMPRINT",FACE,{"disambiguationData":[TD([[makeQuery(id+"F15.imprint","IMPRINT",EDGE,{"derivedFrom":sQuery(id+"F15.wireOp",EDGE,"E24.1.3.0")}),1.0]])]});
            var Q6;
            Q6=makeQuery(id+"F16.imprint","IMPRINT",FACE,{"disambiguationData":[TD([[makeQuery(id+"F16.imprint","IMPRINT",EDGE,{"derivedFrom":sQuery(id+"F16.wireOp",EDGE,"E28.2.0")}),1.0]])]});
            var Q7;
            Q7=makeQuery(id+"F17.imprint","IMPRINT",FACE,{"disambiguationData":[TD([[makeQuery(id+"F17.imprint","IMPRINT",EDGE,{"derivedFrom":sQuery(id+"F17.wireOp",EDGE,"E33.1.0")}),1.0]])]});
            var Q8;
            Q8=makeQuery(id+"F18.imprint","IMPRINT",FACE,{"disambiguationData":[TD([[makeQuery(id+"F18.imprint","IMPRINT",EDGE,{"derivedFrom":sQuery(id+"F18.wireOp",EDGE,"E37")}),1.0]])]});
            var Q9;
            Q9=makeQuery(id+"F19.imprint","IMPRINT",FACE,{"disambiguationData":[TD([[makeQuery(id+"F19.imprint","IMPRINT",EDGE,{"derivedFrom":sQuery(id+"F19.wireOp",EDGE,"E44.1.11.0")}),1.0]])]});
            var Q10;
            Q10=makeQuery(id+"F20.imprint","IMPRINT",FACE,{"disambiguationData":[TD([[makeQuery(id+"F20.imprint","IMPRINT",EDGE,{"derivedFrom":sQuery(id+"F20.wireOp",EDGE,"E49.1.10.0")}),1.0]])]});
            var Q11;
            Q11=makeQuery(id+"F21.imprint","IMPRINT",FACE,{"disambiguationData":[TD([[makeQuery(id+"F21.imprint","IMPRINT",EDGE,{"derivedFrom":sQuery(id+"F21.wireOp",EDGE,"E54.1.9.0")}),1.0]])]});
            var Q12;
            Q12=makeQuery(id+"F22.imprint","IMPRINT",FACE,{"disambiguationData":[TD([[makeQuery(id+"F22.imprint","IMPRINT",EDGE,{"derivedFrom":sQuery(id+"F22.wireOp",EDGE,"E59.1.8.0")}),1.0]])]});
            loft(context, id + "F28", {"operationType" : NewBodyOperationType.ADD, "sheetProfilesArray" : [{ "sheetProfileEntities" : qUnion([Q1]) }, { "sheetProfileEntities" : qUnion([Q2]) }, { "sheetProfileEntities" : qUnion([Q3]) }, { "sheetProfileEntities" : qUnion([Q4]) }, { "sheetProfileEntities" : qUnion([Q5]) }, { "sheetProfileEntities" : qUnion([Q6]) }, { "sheetProfileEntities" : qUnion([Q7]) }, { "sheetProfileEntities" : qUnion([Q8]) }, { "sheetProfileEntities" : qUnion([Q9]) }, { "sheetProfileEntities" : qUnion([Q10]) }, { "sheetProfileEntities" : qUnion([Q11]) }, { "sheetProfileEntities" : qUnion([Q12]) }]});
        }
        {
            var Q1;
            Q1=makeQuery(id+"F11.imprint","IMPRINT",FACE,{"disambiguationData":[TD([[makeQuery(id+"F11.imprint","IMPRINT",EDGE,{"derivedFrom":sQuery(id+"F11.wireOp",EDGE,"E4.1.6.0")}),1.0]])]});
            var Q2;
            Q2=makeQuery(id+"F12.imprint","IMPRINT",FACE,{"disambiguationData":[TD([[makeQuery(id+"F12.imprint","IMPRINT",EDGE,{"derivedFrom":sQuery(id+"F12.wireOp",EDGE,"E9.1.5.0")}),1.0]])]});
            var Q3;
            Q3=makeQuery(id+"F13.imprint","IMPRINT",FACE,{"disambiguationData":[TD([[makeQuery(id+"F13.imprint","IMPRINT",EDGE,{"derivedFrom":sQuery(id+"F13.wireOp",EDGE,"E14.1.4.0")}),1.0]])]});
            var Q4;
            Q4=makeQuery(id+"F14.imprint","IMPRINT",FACE,{"disambiguationData":[TD([[makeQuery(id+"F14.imprint","IMPRINT",EDGE,{"derivedFrom":sQuery(id+"F14.wireOp",EDGE,"E19.1.3.0")}),1.0]])]});
            var Q5;
            Q5=makeQuery(id+"F15.imprint","IMPRINT",FACE,{"disambiguationData":[TD([[makeQuery(id+"F15.imprint","IMPRINT",EDGE,{"derivedFrom":sQuery(id+"F15.wireOp",EDGE,"E23.2.0")}),1.0]])]});
            var Q6;
            Q6=makeQuery(id+"F16.imprint","IMPRINT",FACE,{"disambiguationData":[TD([[makeQuery(id+"F16.imprint","IMPRINT",EDGE,{"derivedFrom":sQuery(id+"F16.wireOp",EDGE,"E28.1.0")}),1.0]])]});
            var Q7;
            Q7=makeQuery(id+"F17.imprint","IMPRINT",FACE,{"disambiguationData":[TD([[makeQuery(id+"F17.imprint","IMPRINT",EDGE,{"derivedFrom":sQuery(id+"F17.wireOp",EDGE,"E32")}),1.0]])]});
            var Q8;
            Q8=makeQuery(id+"F18.imprint","IMPRINT",FACE,{"disambiguationData":[TD([[makeQuery(id+"F18.imprint","IMPRINT",EDGE,{"derivedFrom":sQuery(id+"F18.wireOp",EDGE,"E39.1.11.0")}),1.0]])]});
            var Q9;
            Q9=makeQuery(id+"F19.imprint","IMPRINT",FACE,{"disambiguationData":[TD([[makeQuery(id+"F19.imprint","IMPRINT",EDGE,{"derivedFrom":sQuery(id+"F19.wireOp",EDGE,"E44.1.10.0")}),1.0]])]});
            var Q10;
            Q10=makeQuery(id+"F20.imprint","IMPRINT",FACE,{"disambiguationData":[TD([[makeQuery(id+"F20.imprint","IMPRINT",EDGE,{"derivedFrom":sQuery(id+"F20.wireOp",EDGE,"E49.1.9.0")}),1.0]])]});
            var Q11;
            Q11=makeQuery(id+"F21.imprint","IMPRINT",FACE,{"disambiguationData":[TD([[makeQuery(id+"F21.imprint","IMPRINT",EDGE,{"derivedFrom":sQuery(id+"F21.wireOp",EDGE,"E54.1.8.0")}),1.0]])]});
            var Q12;
            Q12=makeQuery(id+"F22.imprint","IMPRINT",FACE,{"disambiguationData":[TD([[makeQuery(id+"F22.imprint","IMPRINT",EDGE,{"derivedFrom":sQuery(id+"F22.wireOp",EDGE,"E59.1.7.0")}),1.0]])]});
            loft(context, id + "F29", {"operationType" : NewBodyOperationType.ADD, "sheetProfilesArray" : [{ "sheetProfileEntities" : qUnion([Q1]) }, { "sheetProfileEntities" : qUnion([Q2]) }, { "sheetProfileEntities" : qUnion([Q3]) }, { "sheetProfileEntities" : qUnion([Q4]) }, { "sheetProfileEntities" : qUnion([Q5]) }, { "sheetProfileEntities" : qUnion([Q6]) }, { "sheetProfileEntities" : qUnion([Q7]) }, { "sheetProfileEntities" : qUnion([Q8]) }, { "sheetProfileEntities" : qUnion([Q9]) }, { "sheetProfileEntities" : qUnion([Q10]) }, { "sheetProfileEntities" : qUnion([Q11]) }, { "sheetProfileEntities" : qUnion([Q12]) }]});
        }
        {
            var Q1;
            Q1=makeQuery(id+"F11.imprint","IMPRINT",FACE,{"disambiguationData":[TD([[makeQuery(id+"F11.imprint","IMPRINT",EDGE,{"derivedFrom":sQuery(id+"F11.wireOp",EDGE,"E4.1.5.0")}),1.0]])]});
            var Q2;
            Q2=makeQuery(id+"F12.imprint","IMPRINT",FACE,{"disambiguationData":[TD([[makeQuery(id+"F12.imprint","IMPRINT",EDGE,{"derivedFrom":sQuery(id+"F12.wireOp",EDGE,"E9.1.4.0")}),1.0]])]});
            var Q3;
            Q3=makeQuery(id+"F13.imprint","IMPRINT",FACE,{"disambiguationData":[TD([[makeQuery(id+"F13.imprint","IMPRINT",EDGE,{"derivedFrom":sQuery(id+"F13.wireOp",EDGE,"E14.1.3.0")}),1.0]])]});
            var Q4;
            Q4=makeQuery(id+"F14.imprint","IMPRINT",FACE,{"disambiguationData":[TD([[makeQuery(id+"F14.imprint","IMPRINT",EDGE,{"derivedFrom":sQuery(id+"F14.wireOp",EDGE,"E18.2.0")}),1.0]])]});
            var Q5;
            Q5=makeQuery(id+"F15.imprint","IMPRINT",FACE,{"disambiguationData":[TD([[makeQuery(id+"F15.imprint","IMPRINT",EDGE,{"derivedFrom":sQuery(id+"F15.wireOp",EDGE,"E23.1.0")}),1.0]])]});
            var Q6;
            Q6=makeQuery(id+"F16.imprint","IMPRINT",FACE,{"disambiguationData":[TD([[makeQuery(id+"F16.imprint","IMPRINT",EDGE,{"derivedFrom":sQuery(id+"F16.wireOp",EDGE,"E27")}),1.0]])]});
            var Q7;
            Q7=makeQuery(id+"F17.imprint","IMPRINT",FACE,{"disambiguationData":[TD([[makeQuery(id+"F17.imprint","IMPRINT",EDGE,{"derivedFrom":sQuery(id+"F17.wireOp",EDGE,"E34.1.11.0")}),1.0]])]});
            var Q8;
            Q8=makeQuery(id+"F18.imprint","IMPRINT",FACE,{"disambiguationData":[TD([[makeQuery(id+"F18.imprint","IMPRINT",EDGE,{"derivedFrom":sQuery(id+"F18.wireOp",EDGE,"E39.1.10.0")}),1.0]])]});
            var Q9;
            Q9=makeQuery(id+"F19.imprint","IMPRINT",FACE,{"disambiguationData":[TD([[makeQuery(id+"F19.imprint","IMPRINT",EDGE,{"derivedFrom":sQuery(id+"F19.wireOp",EDGE,"E44.1.9.0")}),1.0]])]});
            var Q10;
            Q10=makeQuery(id+"F20.imprint","IMPRINT",FACE,{"disambiguationData":[TD([[makeQuery(id+"F20.imprint","IMPRINT",EDGE,{"derivedFrom":sQuery(id+"F20.wireOp",EDGE,"E49.1.8.0")}),1.0]])]});
            var Q11;
            Q11=makeQuery(id+"F21.imprint","IMPRINT",FACE,{"disambiguationData":[TD([[makeQuery(id+"F21.imprint","IMPRINT",EDGE,{"derivedFrom":sQuery(id+"F21.wireOp",EDGE,"E54.1.7.0")}),1.0]])]});
            var Q12;
            Q12=makeQuery(id+"F22.imprint","IMPRINT",FACE,{"disambiguationData":[TD([[makeQuery(id+"F22.imprint","IMPRINT",EDGE,{"derivedFrom":sQuery(id+"F22.wireOp",EDGE,"E59.1.6.0")}),1.0]])]});
            loft(context, id + "F30", {"operationType" : NewBodyOperationType.ADD, "sheetProfilesArray" : [{ "sheetProfileEntities" : qUnion([Q1]) }, { "sheetProfileEntities" : qUnion([Q2]) }, { "sheetProfileEntities" : qUnion([Q3]) }, { "sheetProfileEntities" : qUnion([Q4]) }, { "sheetProfileEntities" : qUnion([Q5]) }, { "sheetProfileEntities" : qUnion([Q6]) }, { "sheetProfileEntities" : qUnion([Q7]) }, { "sheetProfileEntities" : qUnion([Q8]) }, { "sheetProfileEntities" : qUnion([Q9]) }, { "sheetProfileEntities" : qUnion([Q10]) }, { "sheetProfileEntities" : qUnion([Q11]) }, { "sheetProfileEntities" : qUnion([Q12]) }]});
        }
        {
            var Q1;
            Q1=makeQuery(id+"F11.imprint","IMPRINT",FACE,{"disambiguationData":[TD([[makeQuery(id+"F11.imprint","IMPRINT",EDGE,{"derivedFrom":sQuery(id+"F11.wireOp",EDGE,"E4.1.4.0")}),1.0]])]});
            var Q2;
            Q2=makeQuery(id+"F12.imprint","IMPRINT",FACE,{"disambiguationData":[TD([[makeQuery(id+"F12.imprint","IMPRINT",EDGE,{"derivedFrom":sQuery(id+"F12.wireOp",EDGE,"E9.1.3.0")}),1.0]])]});
            var Q3;
            Q3=makeQuery(id+"F13.imprint","IMPRINT",FACE,{"disambiguationData":[TD([[makeQuery(id+"F13.imprint","IMPRINT",EDGE,{"derivedFrom":sQuery(id+"F13.wireOp",EDGE,"E13.2.0")}),1.0]])]});
            var Q4;
            Q4=makeQuery(id+"F14.imprint","IMPRINT",FACE,{"disambiguationData":[TD([[makeQuery(id+"F14.imprint","IMPRINT",EDGE,{"derivedFrom":sQuery(id+"F14.wireOp",EDGE,"E18.1.0")}),1.0]])]});
            var Q5;
            Q5=makeQuery(id+"F15.imprint","IMPRINT",FACE,{"disambiguationData":[TD([[makeQuery(id+"F15.imprint","IMPRINT",EDGE,{"derivedFrom":sQuery(id+"F15.wireOp",EDGE,"E22")}),1.0]])]});
            var Q6;
            Q6=makeQuery(id+"F16.imprint","IMPRINT",FACE,{"disambiguationData":[TD([[makeQuery(id+"F16.imprint","IMPRINT",EDGE,{"derivedFrom":sQuery(id+"F16.wireOp",EDGE,"E29.1.11.0")}),1.0]])]});
            var Q7;
            Q7=makeQuery(id+"F17.imprint","IMPRINT",FACE,{"disambiguationData":[TD([[makeQuery(id+"F17.imprint","IMPRINT",EDGE,{"derivedFrom":sQuery(id+"F17.wireOp",EDGE,"E34.1.10.0")}),1.0]])]});
            var Q8;
            Q8=makeQuery(id+"F18.imprint","IMPRINT",FACE,{"disambiguationData":[TD([[makeQuery(id+"F18.imprint","IMPRINT",EDGE,{"derivedFrom":sQuery(id+"F18.wireOp",EDGE,"E39.1.9.0")}),1.0]])]});
            var Q9;
            Q9=makeQuery(id+"F19.imprint","IMPRINT",FACE,{"disambiguationData":[TD([[makeQuery(id+"F19.imprint","IMPRINT",EDGE,{"derivedFrom":sQuery(id+"F19.wireOp",EDGE,"E44.1.8.0")}),1.0]])]});
            var Q10;
            Q10=makeQuery(id+"F20.imprint","IMPRINT",FACE,{"disambiguationData":[TD([[makeQuery(id+"F20.imprint","IMPRINT",EDGE,{"derivedFrom":sQuery(id+"F20.wireOp",EDGE,"E49.1.7.0")}),1.0]])]});
            var Q11;
            Q11=makeQuery(id+"F21.imprint","IMPRINT",FACE,{"disambiguationData":[TD([[makeQuery(id+"F21.imprint","IMPRINT",EDGE,{"derivedFrom":sQuery(id+"F21.wireOp",EDGE,"E54.1.6.0")}),1.0]])]});
            var Q12;
            Q12=makeQuery(id+"F22.imprint","IMPRINT",FACE,{"disambiguationData":[TD([[makeQuery(id+"F22.imprint","IMPRINT",EDGE,{"derivedFrom":sQuery(id+"F22.wireOp",EDGE,"E59.1.5.0")}),1.0]])]});
            loft(context, id + "F31", {"operationType" : NewBodyOperationType.ADD, "sheetProfilesArray" : [{ "sheetProfileEntities" : qUnion([Q1]) }, { "sheetProfileEntities" : qUnion([Q2]) }, { "sheetProfileEntities" : qUnion([Q3]) }, { "sheetProfileEntities" : qUnion([Q4]) }, { "sheetProfileEntities" : qUnion([Q5]) }, { "sheetProfileEntities" : qUnion([Q6]) }, { "sheetProfileEntities" : qUnion([Q7]) }, { "sheetProfileEntities" : qUnion([Q8]) }, { "sheetProfileEntities" : qUnion([Q9]) }, { "sheetProfileEntities" : qUnion([Q10]) }, { "sheetProfileEntities" : qUnion([Q11]) }, { "sheetProfileEntities" : qUnion([Q12]) }]});
        }
        {
            var Q1;
            Q1=makeQuery(id+"F11.imprint","IMPRINT",FACE,{"disambiguationData":[TD([[makeQuery(id+"F11.imprint","IMPRINT",EDGE,{"derivedFrom":sQuery(id+"F11.wireOp",EDGE,"E4.1.3.0")}),1.0]])]});
            var Q2;
            Q2=makeQuery(id+"F12.imprint","IMPRINT",FACE,{"disambiguationData":[TD([[makeQuery(id+"F12.imprint","IMPRINT",EDGE,{"derivedFrom":sQuery(id+"F12.wireOp",EDGE,"E8.2.0")}),1.0]])]});
            var Q3;
            Q3=makeQuery(id+"F13.imprint","IMPRINT",FACE,{"disambiguationData":[TD([[makeQuery(id+"F13.imprint","IMPRINT",EDGE,{"derivedFrom":sQuery(id+"F13.wireOp",EDGE,"E13.1.0")}),1.0]])]});
            var Q4;
            Q4=makeQuery(id+"F14.imprint","IMPRINT",FACE,{"disambiguationData":[TD([[makeQuery(id+"F14.imprint","IMPRINT",EDGE,{"derivedFrom":sQuery(id+"F14.wireOp",EDGE,"E17")}),1.0]])]});
            var Q5;
            Q5=makeQuery(id+"F15.imprint","IMPRINT",FACE,{"disambiguationData":[TD([[makeQuery(id+"F15.imprint","IMPRINT",EDGE,{"derivedFrom":sQuery(id+"F15.wireOp",EDGE,"E24.1.11.0")}),1.0]])]});
            var Q6;
            Q6=makeQuery(id+"F16.imprint","IMPRINT",FACE,{"disambiguationData":[TD([[makeQuery(id+"F16.imprint","IMPRINT",EDGE,{"derivedFrom":sQuery(id+"F16.wireOp",EDGE,"E29.1.10.0")}),1.0]])]});
            var Q7;
            Q7=makeQuery(id+"F17.imprint","IMPRINT",FACE,{"disambiguationData":[TD([[makeQuery(id+"F17.imprint","IMPRINT",EDGE,{"derivedFrom":sQuery(id+"F17.wireOp",EDGE,"E34.1.9.0")}),1.0]])]});
            var Q8;
            Q8=makeQuery(id+"F18.imprint","IMPRINT",FACE,{"disambiguationData":[TD([[makeQuery(id+"F18.imprint","IMPRINT",EDGE,{"derivedFrom":sQuery(id+"F18.wireOp",EDGE,"E39.1.8.0")}),1.0]])]});
            var Q9;
            Q9=makeQuery(id+"F19.imprint","IMPRINT",FACE,{"disambiguationData":[TD([[makeQuery(id+"F19.imprint","IMPRINT",EDGE,{"derivedFrom":sQuery(id+"F19.wireOp",EDGE,"E44.1.7.0")}),1.0]])]});
            var Q10;
            Q10=makeQuery(id+"F20.imprint","IMPRINT",FACE,{"disambiguationData":[TD([[makeQuery(id+"F20.imprint","IMPRINT",EDGE,{"derivedFrom":sQuery(id+"F20.wireOp",EDGE,"E49.1.6.0")}),1.0]])]});
            var Q11;
            Q11=makeQuery(id+"F21.imprint","IMPRINT",FACE,{"disambiguationData":[TD([[makeQuery(id+"F21.imprint","IMPRINT",EDGE,{"derivedFrom":sQuery(id+"F21.wireOp",EDGE,"E54.1.5.0")}),1.0]])]});
            var Q12;
            Q12=makeQuery(id+"F22.imprint","IMPRINT",FACE,{"disambiguationData":[TD([[makeQuery(id+"F22.imprint","IMPRINT",EDGE,{"derivedFrom":sQuery(id+"F22.wireOp",EDGE,"E59.1.4.0")}),1.0]])]});
            loft(context, id + "F32", {"operationType" : NewBodyOperationType.ADD, "sheetProfilesArray" : [{ "sheetProfileEntities" : qUnion([Q1]) }, { "sheetProfileEntities" : qUnion([Q2]) }, { "sheetProfileEntities" : qUnion([Q3]) }, { "sheetProfileEntities" : qUnion([Q4]) }, { "sheetProfileEntities" : qUnion([Q5]) }, { "sheetProfileEntities" : qUnion([Q6]) }, { "sheetProfileEntities" : qUnion([Q7]) }, { "sheetProfileEntities" : qUnion([Q8]) }, { "sheetProfileEntities" : qUnion([Q9]) }, { "sheetProfileEntities" : qUnion([Q10]) }, { "sheetProfileEntities" : qUnion([Q11]) }, { "sheetProfileEntities" : qUnion([Q12]) }]});
        }
        {
            var Q1;
            Q1=makeQuery(id+"F11.imprint","IMPRINT",FACE,{"disambiguationData":[TD([[makeQuery(id+"F11.imprint","IMPRINT",EDGE,{"derivedFrom":sQuery(id+"F11.wireOp",EDGE,"E3.2.0")}),1.0]])]});
            var Q2;
            Q2=makeQuery(id+"F12.imprint","IMPRINT",FACE,{"disambiguationData":[TD([[makeQuery(id+"F12.imprint","IMPRINT",EDGE,{"derivedFrom":sQuery(id+"F12.wireOp",EDGE,"E8.1.0")}),1.0]])]});
            var Q3;
            Q3=makeQuery(id+"F13.imprint","IMPRINT",FACE,{"disambiguationData":[TD([[makeQuery(id+"F13.imprint","IMPRINT",EDGE,{"derivedFrom":sQuery(id+"F13.wireOp",EDGE,"E12")}),1.0]])]});
            var Q4;
            Q4=makeQuery(id+"F14.imprint","IMPRINT",FACE,{"disambiguationData":[TD([[makeQuery(id+"F14.imprint","IMPRINT",EDGE,{"derivedFrom":sQuery(id+"F14.wireOp",EDGE,"E19.1.11.0")}),1.0]])]});
            var Q5;
            Q5=makeQuery(id+"F15.imprint","IMPRINT",FACE,{"disambiguationData":[TD([[makeQuery(id+"F15.imprint","IMPRINT",EDGE,{"derivedFrom":sQuery(id+"F15.wireOp",EDGE,"E24.1.10.0")}),1.0]])]});
            var Q6;
            Q6=makeQuery(id+"F16.imprint","IMPRINT",FACE,{"disambiguationData":[TD([[makeQuery(id+"F16.imprint","IMPRINT",EDGE,{"derivedFrom":sQuery(id+"F16.wireOp",EDGE,"E29.1.9.0")}),1.0]])]});
            var Q7;
            Q7=makeQuery(id+"F17.imprint","IMPRINT",FACE,{"disambiguationData":[TD([[makeQuery(id+"F17.imprint","IMPRINT",EDGE,{"derivedFrom":sQuery(id+"F17.wireOp",EDGE,"E34.1.8.0")}),1.0]])]});
            var Q8;
            Q8=makeQuery(id+"F18.imprint","IMPRINT",FACE,{"disambiguationData":[TD([[makeQuery(id+"F18.imprint","IMPRINT",EDGE,{"derivedFrom":sQuery(id+"F18.wireOp",EDGE,"E39.1.7.0")}),1.0]])]});
            var Q9;
            Q9=makeQuery(id+"F19.imprint","IMPRINT",FACE,{"disambiguationData":[TD([[makeQuery(id+"F19.imprint","IMPRINT",EDGE,{"derivedFrom":sQuery(id+"F19.wireOp",EDGE,"E44.1.6.0")}),1.0]])]});
            var Q10;
            Q10=makeQuery(id+"F20.imprint","IMPRINT",FACE,{"disambiguationData":[TD([[makeQuery(id+"F20.imprint","IMPRINT",EDGE,{"derivedFrom":sQuery(id+"F20.wireOp",EDGE,"E49.1.5.0")}),1.0]])]});
            var Q11;
            Q11=makeQuery(id+"F21.imprint","IMPRINT",FACE,{"disambiguationData":[TD([[makeQuery(id+"F21.imprint","IMPRINT",EDGE,{"derivedFrom":sQuery(id+"F21.wireOp",EDGE,"E54.1.4.0")}),1.0]])]});
            var Q12;
            Q12=makeQuery(id+"F22.imprint","IMPRINT",FACE,{"disambiguationData":[TD([[makeQuery(id+"F22.imprint","IMPRINT",EDGE,{"derivedFrom":sQuery(id+"F22.wireOp",EDGE,"E59.1.3.0")}),1.0]])]});
            loft(context, id + "F33", {"operationType" : NewBodyOperationType.ADD, "sheetProfilesArray" : [{ "sheetProfileEntities" : qUnion([Q1]) }, { "sheetProfileEntities" : qUnion([Q2]) }, { "sheetProfileEntities" : qUnion([Q3]) }, { "sheetProfileEntities" : qUnion([Q4]) }, { "sheetProfileEntities" : qUnion([Q5]) }, { "sheetProfileEntities" : qUnion([Q6]) }, { "sheetProfileEntities" : qUnion([Q7]) }, { "sheetProfileEntities" : qUnion([Q8]) }, { "sheetProfileEntities" : qUnion([Q9]) }, { "sheetProfileEntities" : qUnion([Q10]) }, { "sheetProfileEntities" : qUnion([Q11]) }, { "sheetProfileEntities" : qUnion([Q12]) }]});
        }
        {
            var Q1;
            Q1=makeQuery(id+"F11.imprint","IMPRINT",FACE,{"disambiguationData":[TD([[makeQuery(id+"F11.imprint","IMPRINT",EDGE,{"derivedFrom":sQuery(id+"F11.wireOp",EDGE,"E3.1.0")}),1.0]])]});
            var Q2;
            Q2=makeQuery(id+"F12.imprint","IMPRINT",FACE,{"disambiguationData":[TD([[makeQuery(id+"F12.imprint","IMPRINT",EDGE,{"derivedFrom":sQuery(id+"F12.wireOp",EDGE,"E7")}),1.0]])]});
            var Q3;
            Q3=makeQuery(id+"F13.imprint","IMPRINT",FACE,{"disambiguationData":[TD([[makeQuery(id+"F13.imprint","IMPRINT",EDGE,{"derivedFrom":sQuery(id+"F13.wireOp",EDGE,"E14.1.11.0")}),1.0]])]});
            var Q4;
            Q4=makeQuery(id+"F14.imprint","IMPRINT",FACE,{"disambiguationData":[TD([[makeQuery(id+"F14.imprint","IMPRINT",EDGE,{"derivedFrom":sQuery(id+"F14.wireOp",EDGE,"E19.1.10.0")}),1.0]])]});
            var Q5;
            Q5=makeQuery(id+"F15.imprint","IMPRINT",FACE,{"disambiguationData":[TD([[makeQuery(id+"F15.imprint","IMPRINT",EDGE,{"derivedFrom":sQuery(id+"F15.wireOp",EDGE,"E24.1.9.0")}),1.0]])]});
            var Q6;
            Q6=makeQuery(id+"F16.imprint","IMPRINT",FACE,{"disambiguationData":[TD([[makeQuery(id+"F16.imprint","IMPRINT",EDGE,{"derivedFrom":sQuery(id+"F16.wireOp",EDGE,"E29.1.8.0")}),1.0]])]});
            var Q7;
            Q7=makeQuery(id+"F17.imprint","IMPRINT",FACE,{"disambiguationData":[TD([[makeQuery(id+"F17.imprint","IMPRINT",EDGE,{"derivedFrom":sQuery(id+"F17.wireOp",EDGE,"E34.1.7.0")}),1.0]])]});
            var Q8;
            Q8=makeQuery(id+"F18.imprint","IMPRINT",FACE,{"disambiguationData":[TD([[makeQuery(id+"F18.imprint","IMPRINT",EDGE,{"derivedFrom":sQuery(id+"F18.wireOp",EDGE,"E39.1.6.0")}),1.0]])]});
            var Q9;
            Q9=makeQuery(id+"F20.imprint","IMPRINT",FACE,{"disambiguationData":[TD([[makeQuery(id+"F20.imprint","IMPRINT",EDGE,{"derivedFrom":sQuery(id+"F20.wireOp",EDGE,"E49.1.4.0")}),1.0]])]});
            var Q10;
            Q10=makeQuery(id+"F21.imprint","IMPRINT",FACE,{"disambiguationData":[TD([[makeQuery(id+"F21.imprint","IMPRINT",EDGE,{"derivedFrom":sQuery(id+"F21.wireOp",EDGE,"E54.1.3.0")}),1.0]])]});
            var Q11;
            Q11=makeQuery(id+"F22.imprint","IMPRINT",FACE,{"disambiguationData":[TD([[makeQuery(id+"F22.imprint","IMPRINT",EDGE,{"derivedFrom":sQuery(id+"F22.wireOp",EDGE,"E58.2.0")}),1.0]])]});
            loft(context, id + "F34", {"operationType" : NewBodyOperationType.ADD, "sheetProfilesArray" : [{ "sheetProfileEntities" : qUnion([Q1]) }, { "sheetProfileEntities" : qUnion([Q2]) }, { "sheetProfileEntities" : qUnion([Q3]) }, { "sheetProfileEntities" : qUnion([Q4]) }, { "sheetProfileEntities" : qUnion([Q5]) }, { "sheetProfileEntities" : qUnion([Q6]) }, { "sheetProfileEntities" : qUnion([Q7]) }, { "sheetProfileEntities" : qUnion([Q8]) }, { "sheetProfileEntities" : qUnion([Q9]) }, { "sheetProfileEntities" : qUnion([Q10]) }, { "sheetProfileEntities" : qUnion([Q11]) }]});
        }
    });
